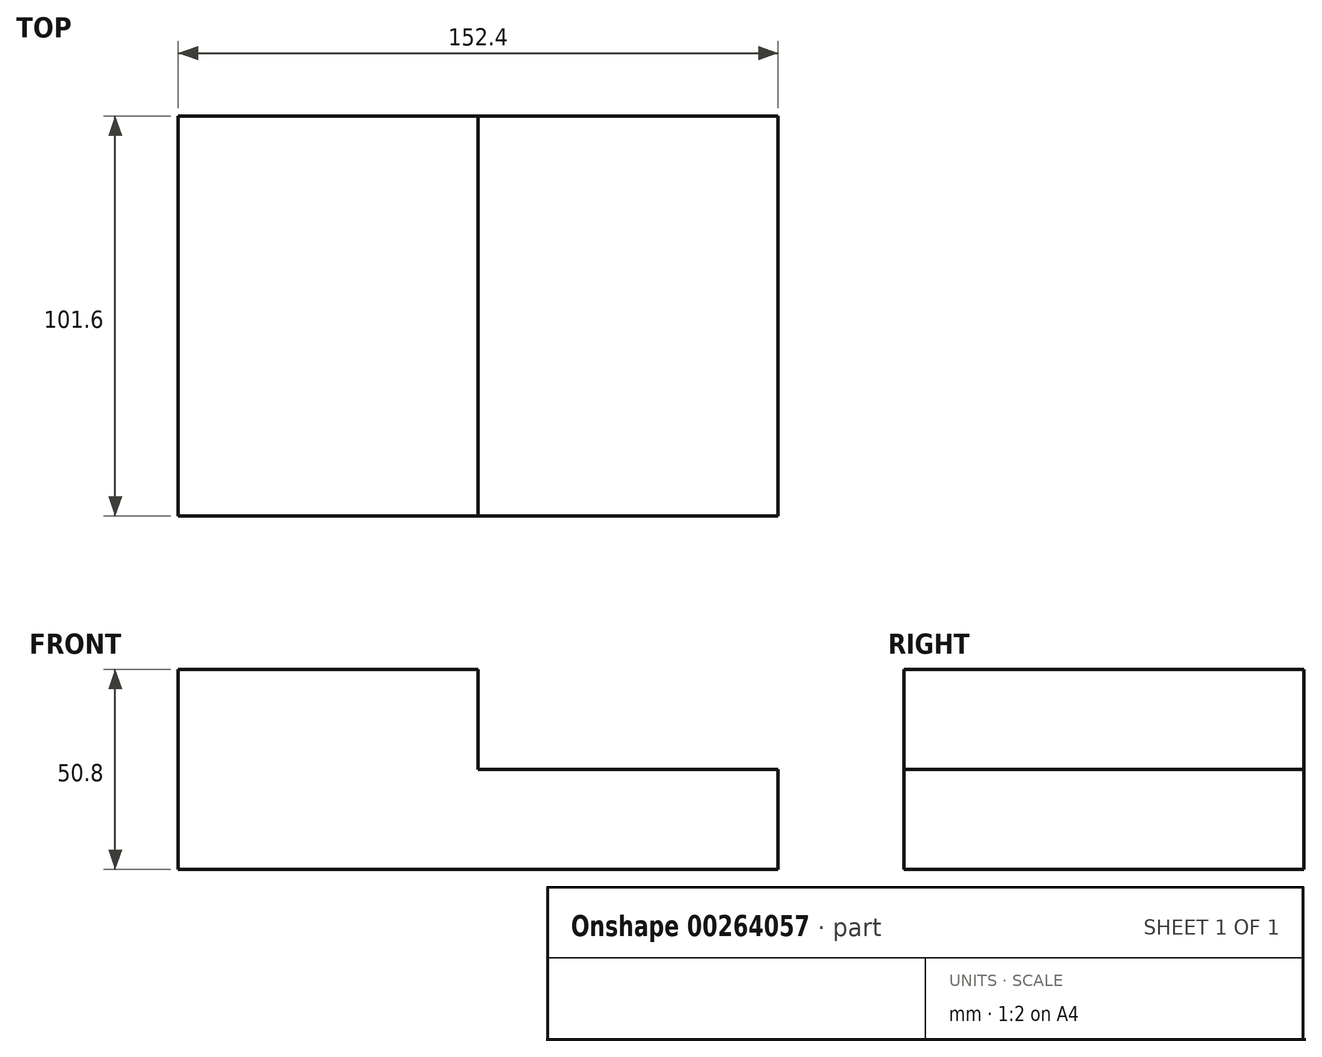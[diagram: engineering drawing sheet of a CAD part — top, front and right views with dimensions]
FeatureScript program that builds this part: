
annotation { "Feature Type Name" : "Feature", "Feature Type Description" : "" }
export const myFeature = defineFeature(function(context is Context, id is Id, definition is map)
    precondition{}
    {
        {
            var Q0;
            Q0=qCreatedBy(makeId("Front.planeOp"),FACE);
            var sketch = newSketch(context, id + "F0", { "sketchPlane" : qUnion([Q0])});
            skLineSegment(sketch, "E0", {"start": v(-65.98, 50.8) * mm, "end": v(-65.98, 0) * mm});
            skLineSegment(sketch, "E1", {"start": v(-65.98, 0) * mm, "end": v(86.42, 0) * mm});
            skLineSegment(sketch, "E2", {"start": v(86.42, 0) * mm, "end": v(86.42, 25.4) * mm});
            skLineSegment(sketch, "E3", {"start": v(86.42, 25.4) * mm, "end": v(10.22, 25.4) * mm});
            skLineSegment(sketch, "E4", {"start": v(-65.98, 50.8) * mm, "end": v(10.22, 50.8) * mm});
            skLineSegment(sketch, "E5", {"start": v(10.22, 25.4) * mm, "end": v(10.22, 50.8) * mm});
            skSolve(sketch);
        }
        {
            var Q0;
            Q0=makeQuery(id+"F0.imprint","IMPRINT",FACE,{"disambiguationData":[TD([[makeQuery(id+"F0.imprint","IMPRINT",EDGE,{"derivedFrom":sQuery(id+"F0.wireOp",EDGE,"E0")}),1.0]])]});
            extrude(context, id + "F1", {"entities" : qUnion([Q0]), "depth" : 25.4 * mm});
        }
        {
            var Q0;
            Q0=makeQuery(id+"F1.opExtrude","CAP_FACE",FACE,{"disambiguationData":[OSD([sQuery(id+"F0.wireOp",EDGE,"E0"),sQuery(id+"F0.wireOp",EDGE,"E1"),sQuery(id+"F0.wireOp",EDGE,"E2"),sQuery(id+"F0.wireOp",EDGE,"E3"),sQuery(id+"F0.wireOp",EDGE,"E4"),sQuery(id+"F0.wireOp",EDGE,"E5")])],"isStart":false});
            extrude(context, id + "F2", {"entities" : qUnion([Q0]), "operationType" : NewBodyOperationType.ADD, "depth" : 76.2 * mm});
        }
    });
